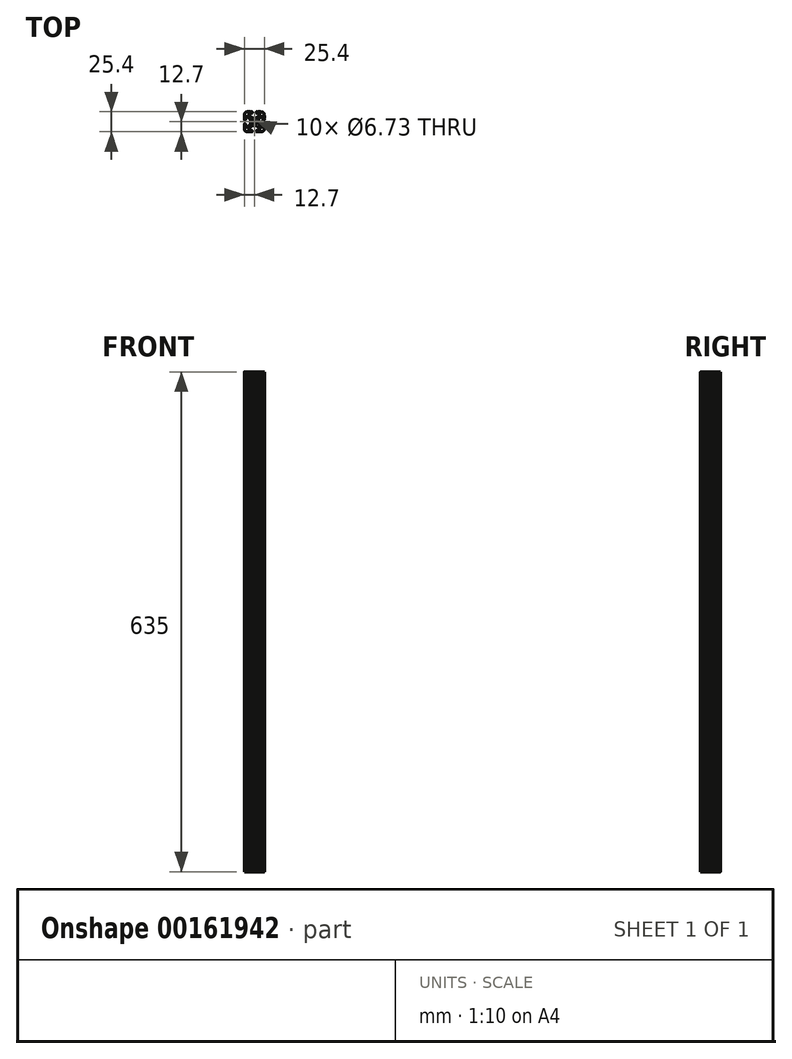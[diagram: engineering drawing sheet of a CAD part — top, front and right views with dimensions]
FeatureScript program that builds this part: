
annotation { "Feature Type Name" : "Feature", "Feature Type Description" : "" }
export const myFeature = defineFeature(function(context is Context, id is Id, definition is map)
    precondition{}
    {
        {
            var Q0;
            Q0=qCreatedBy(makeId("Top.planeOp"),FACE);
            var sketch = newSketch(context, id + "F0", { "sketchPlane" : qUnion([Q0])});
            skCircle(sketch, "E0", {"center": v(-12.7, 12.7) * mm, "radius": 3.36 * mm});
            skLineSegment(sketch, "E1.bottom", {"start": v(-11.24, 17.64) * mm, "end": v(-14.16, 17.64) * mm});
            skLineSegment(sketch, "E1.top", {"start": v(-11.24, 7.76) * mm, "end": v(-14.16, 7.76) * mm});
            skLineSegment(sketch, "E1.left", {"start": v(-7.76, 14.16) * mm, "end": v(-7.76, 11.24) * mm});
            skLineSegment(sketch, "E1.right", {"start": v(-17.64, 14.16) * mm, "end": v(-17.64, 11.24) * mm});
            skPoint(sketch, "E2.visualSharp", {"position": v(-25.4, 25.4) * mm});
            skPoint(sketch, "E3.visualSharp", {"position": v(0, 25.4) * mm});
            skPoint(sketch, "E4.visualSharp", {"position": v(0, 0) * mm});
            skPoint(sketch, "E5.visualSharp", {"position": v(-25.4, 0) * mm});
            skLineSegment(sketch, "E6.0", {"start": v(-18.7, 20.6) * mm, "end": v(-16.85, 18.76) * mm});
            skLineSegment(sketch, "E7.0", {"start": v(-20.6, 18.7) * mm, "end": v(-18.76, 16.85) * mm});
            skPoint(sketch, "E8.orphan", {"position": v(-23.85, 1.55) * mm});
            skPoint(sketch, "E9.orphan", {"position": v(-23.85, 23.85) * mm});
            skPoint(sketch, "E10.orphan", {"position": v(-1.55, 23.85) * mm});
            skPoint(sketch, "E11.orphan", {"position": v(-1.55, 1.55) * mm});
            skLineSegment(sketch, "E12", {"start": v(-8.55, 6.64) * mm, "end": v(-6.7, 4.8) * mm});
            skLineSegment(sketch, "E13.0", {"start": v(-18.7, 4.8) * mm, "end": v(-16.85, 6.64) * mm});
            skLineSegment(sketch, "E14.0", {"start": v(-20.6, 6.7) * mm, "end": v(-18.76, 8.55) * mm});
            skLineSegment(sketch, "E15.0", {"start": v(-8.55, 18.76) * mm, "end": v(-6.7, 20.6) * mm});
            skPoint(sketch, "E16.visualSharp", {"position": v(-23.85, 21.95) * mm});
            skArc(sketch, "E16.filletArc", {"start": v(-20.6, 18.7) * mm, "mid": v(-22.68, 19.1) * mm, "end": v(-23.85, 17.35) * mm});
            skPoint(sketch, "E17.visualSharp", {"position": v(-21.95, 23.85) * mm});
            skArc(sketch, "E17.filletArc", {"start": v(-17.35, 23.85) * mm, "mid": v(-19.1, 22.68) * mm, "end": v(-18.7, 20.6) * mm});
            skPoint(sketch, "E18.visualSharp", {"position": v(-5.34, 23.85) * mm});
            skLineSegment(sketch, "E19", {"start": v(-17.35, 23.85) * mm, "end": v(-15.58, 23.85) * mm});
            skLineSegment(sketch, "E20", {"start": v(-23.85, 17.35) * mm, "end": v(-23.85, 15.62) * mm});
            skLineSegment(sketch, "E21", {"start": v(-8.05, 1.55) * mm, "end": v(-9.78, 1.55) * mm});
            skArc(sketch, "E22.filletArc", {"start": v(-6.7, 20.6) * mm, "mid": v(-6.3, 22.68) * mm, "end": v(-8.05, 23.85) * mm});
            skPoint(sketch, "E23.visualSharp", {"position": v(-1.55, 3.45) * mm});
            skPoint(sketch, "E24.visualSharp", {"position": v(-3.45, 1.55) * mm});
            skArc(sketch, "E24.filletArc", {"start": v(-8.05, 1.55) * mm, "mid": v(-6.3, 2.73) * mm, "end": v(-6.7, 4.8) * mm});
            skArc(sketch, "E25.filletArc", {"start": v(-18.7, 4.8) * mm, "mid": v(-19.1, 2.73) * mm, "end": v(-17.35, 1.55) * mm});
            skArc(sketch, "E26.filletArc", {"start": v(-23.85, 8.05) * mm, "mid": v(-22.68, 6.3) * mm, "end": v(-20.6, 6.7) * mm});
            skLineSegment(sketch, "E27.bottom", {"start": v(-4.9, 0) * mm, "end": v(-8.05, 0) * mm});
            skLineSegment(sketch, "E27.top", {"start": v(-4.92, 25.4) * mm, "end": v(-8.05, 25.4) * mm});
            skLineSegment(sketch, "E27.left", {"start": v(0, 4.9) * mm, "end": v(0, 8.05) * mm});
            skLineSegment(sketch, "E27.right", {"start": v(-25.4, 4.9) * mm, "end": v(-25.4, 8.05) * mm});
            skArc(sketch, "E28.filletArc", {"start": v(-25.4, 3.81) * mm, "mid": v(-24.28, 1.12) * mm, "end": v(-21.59, 0) * mm});
            skArc(sketch, "E29.filletArc", {"start": v(-3.81, 0) * mm, "mid": v(-1.12, 1.12) * mm, "end": v(0, 3.8) * mm});
            skArc(sketch, "E30.filletArc", {"start": v(0, 21.59) * mm, "mid": v(-1.12, 24.28) * mm, "end": v(-3.8, 25.4) * mm});
            skArc(sketch, "E31.filletArc", {"start": v(-21.59, 25.4) * mm, "mid": v(-24.28, 24.28) * mm, "end": v(-25.4, 21.59) * mm});
            skPoint(sketch, "E32.newPointA", {"position": v(-17.64, 7.76) * mm});
            skArc(sketch, "E32.filletArc", {"start": v(-14.16, 7.76) * mm, "mid": v(-15.62, 7.47) * mm, "end": v(-16.85, 6.64) * mm});
            skPoint(sketch, "E33.newPointA", {"position": v(-7.76, 7.76) * mm});
            skArc(sketch, "E33.filletArc", {"start": v(-8.55, 6.64) * mm, "mid": v(-9.78, 7.47) * mm, "end": v(-11.24, 7.76) * mm});
            skArc(sketch, "E34.filletArc", {"start": v(-7.76, 11.24) * mm, "mid": v(-7.47, 9.78) * mm, "end": v(-6.64, 8.55) * mm});
            skArc(sketch, "E35.filletArc", {"start": v(-6.64, 16.85) * mm, "mid": v(-7.47, 15.62) * mm, "end": v(-7.76, 14.16) * mm});
            skPoint(sketch, "E36.newPointB", {"position": v(-7.76, 17.64) * mm});
            skArc(sketch, "E36.filletArc", {"start": v(-11.24, 17.64) * mm, "mid": v(-9.78, 17.93) * mm, "end": v(-8.55, 18.76) * mm});
            skPoint(sketch, "E37.newPointB", {"position": v(-17.64, 17.64) * mm});
            skArc(sketch, "E37.filletArc", {"start": v(-16.85, 18.76) * mm, "mid": v(-15.62, 17.93) * mm, "end": v(-14.16, 17.64) * mm});
            skArc(sketch, "E38.filletArc", {"start": v(-17.64, 14.16) * mm, "mid": v(-17.93, 15.62) * mm, "end": v(-18.76, 16.85) * mm});
            skArc(sketch, "E39.filletArc", {"start": v(-18.76, 8.55) * mm, "mid": v(-17.93, 9.78) * mm, "end": v(-17.64, 11.24) * mm});
            skLineSegment(sketch, "E40", {"start": v(-6.64, 8.55) * mm, "end": v(-4.8, 6.7) * mm});
            skPoint(sketch, "E41.visualSharp", {"position": v(-1.55, 21.95) * mm});
            skArc(sketch, "E42.filletArc", {"start": v(-4.8, 6.7) * mm, "mid": v(-2.73, 6.3) * mm, "end": v(-1.55, 8.05) * mm});
            skLineSegment(sketch, "E43", {"start": v(-1.55, 8.05) * mm, "end": v(-1.55, 9.78) * mm});
            skLineSegment(sketch, "E44", {"start": v(-6.64, 16.85) * mm, "end": v(-4.8, 18.7) * mm});
            skArc(sketch, "E45.filletArc", {"start": v(-1.55, 17.35) * mm, "mid": v(-2.73, 19.1) * mm, "end": v(-4.8, 18.7) * mm});
            skArc(sketch, "E46", {"start": v(-23.85, 9.78) * mm, "mid": v(-24.63, 10.56) * mm, "end": v(-25.4, 9.78) * mm});
            skArc(sketch, "E47", {"start": v(-25.4, 15.62) * mm, "mid": v(-24.63, 14.86) * mm, "end": v(-23.85, 15.62) * mm});
            skArc(sketch, "E48", {"start": v(-15.62, 23.85) * mm, "mid": v(-14.83, 24.63) * mm, "end": v(-15.62, 25.4) * mm});
            skArc(sketch, "E49", {"start": v(-9.78, 25.4) * mm, "mid": v(-10.6, 24.63) * mm, "end": v(-9.78, 23.85) * mm});
            skArc(sketch, "E50", {"start": v(-1.55, 15.62) * mm, "mid": v(-0.77, 14.88) * mm, "end": v(0, 15.62) * mm});
            skArc(sketch, "E51", {"start": v(0, 9.78) * mm, "mid": v(-0.77, 10.5) * mm, "end": v(-1.55, 9.78) * mm});
            skArc(sketch, "E52", {"start": v(-9.78, 1.55) * mm, "mid": v(-10.4, 0.77) * mm, "end": v(-9.78, 0) * mm});
            skArc(sketch, "E53", {"start": v(-15.62, 0) * mm, "mid": v(-14.85, 0.77) * mm, "end": v(-15.62, 1.55) * mm});
            skLineSegment(sketch, "E54.trimOffspring", {"start": v(-15.62, 1.55) * mm, "end": v(-17.35, 1.55) * mm});
            skLineSegment(sketch, "E55.trimOffspring", {"start": v(-16.7, 0) * mm, "end": v(-20.5, 0) * mm});
            skLineSegment(sketch, "E56.trimOffspring", {"start": v(-1.55, 15.62) * mm, "end": v(-1.55, 17.35) * mm});
            skLineSegment(sketch, "E57.trimOffspring", {"start": v(0, 15.62) * mm, "end": v(0, 16.26) * mm});
            skLineSegment(sketch, "E58.trimOffspring", {"start": v(-23.85, 9.78) * mm, "end": v(-23.85, 8.05) * mm});
            skLineSegment(sketch, "E59.trimOffspring", {"start": v(-25.4, 15.62) * mm, "end": v(-25.4, 16.26) * mm});
            skLineSegment(sketch, "E60.trimOffspring", {"start": v(-9.86, 23.85) * mm, "end": v(-8.05, 23.85) * mm});
            skLineSegment(sketch, "E61.trimOffspring", {"start": v(-15.58, 25.4) * mm, "end": v(-16.25, 25.4) * mm});
            skPoint(sketch, "E62.start.orphan", {"position": v(-15.62, 17.93) * mm});
            skPoint(sketch, "E63.start.orphan", {"position": v(-9.78, 17.93) * mm});
            skPoint(sketch, "E64.start.orphan", {"position": v(-7.47, 15.62) * mm});
            skPoint(sketch, "E65.start.orphan", {"position": v(-7.47, 9.78) * mm});
            skPoint(sketch, "E66.start.orphan", {"position": v(-17.93, 15.62) * mm});
            skPoint(sketch, "E67.start.orphan", {"position": v(-17.93, 9.78) * mm});
            skPoint(sketch, "E68.start.orphan", {"position": v(-9.78, 7.47) * mm});
            skPoint(sketch, "E69.start.orphan", {"position": v(-15.62, 7.47) * mm});
            skPoint(sketch, "E70.endSnap0", {"position": v(0, 18.6) * mm});
            skPoint(sketch, "E71.startSnap0", {"position": v(-1.55, 8.92) * mm});
            skArc(sketch, "E72", {"start": v(-4.92, 25.4) * mm, "mid": v(-4.37, 24.9) * mm, "end": v(-3.81, 25.4) * mm});
            skArc(sketch, "E73", {"start": v(-9.14, 25.4) * mm, "mid": v(-8.6, 24.86) * mm, "end": v(-8.05, 25.4) * mm});
            skArc(sketch, "E74", {"start": v(-17.35, 25.4) * mm, "mid": v(-16.8, 24.86) * mm, "end": v(-16.25, 25.4) * mm});
            skArc(sketch, "E75", {"start": v(-21.59, 25.4) * mm, "mid": v(-21.04, 24.85) * mm, "end": v(-20.49, 25.4) * mm});
            skLineSegment(sketch, "E76", {"start": v(-25.4, 21.59) * mm, "end": v(-25.4, 20.5) * mm});
            skArc(sketch, "E77", {"start": v(-25.4, 16.26) * mm, "mid": v(-24.84, 16.8) * mm, "end": v(-25.4, 17.35) * mm});
            skArc(sketch, "E78", {"start": v(-25.4, 8.05) * mm, "mid": v(-24.9, 8.6) * mm, "end": v(-25.4, 9.15) * mm});
            skArc(sketch, "E79", {"start": v(-25.4, 3.81) * mm, "mid": v(-24.85, 4.36) * mm, "end": v(-25.4, 4.9) * mm});
            skArc(sketch, "E80", {"start": v(-20.5, 0) * mm, "mid": v(-21.04, 0.55) * mm, "end": v(-21.59, 0) * mm});
            skArc(sketch, "E81", {"start": v(-15.62, 0) * mm, "mid": v(-16.16, 0.54) * mm, "end": v(-16.7, 0) * mm});
            skArc(sketch, "E82", {"start": v(-8.05, 0) * mm, "mid": v(-8.6, 0.55) * mm, "end": v(-9.15, 0) * mm});
            skArc(sketch, "E83", {"start": v(-3.81, 0) * mm, "mid": v(-4.35, 0.54) * mm, "end": v(-4.9, 0) * mm});
            skLineSegment(sketch, "E84.trimOffspring", {"start": v(-17.35, 25.4) * mm, "end": v(-20.49, 25.4) * mm});
            skLineSegment(sketch, "E85.trimOffspring", {"start": v(-25.4, 17.35) * mm, "end": v(-25.4, 21.59) * mm});
            skLineSegment(sketch, "E86.trimOffspring", {"start": v(-25.4, 9.15) * mm, "end": v(-25.4, 9.78) * mm});
            skLineSegment(sketch, "E87.trimOffspring", {"start": v(-9.15, 0) * mm, "end": v(-9.78, 0) * mm});
            skArc(sketch, "E88", {"start": v(0, 4.9) * mm, "mid": v(-0.54, 4.36) * mm, "end": v(0, 3.8) * mm});
            skArc(sketch, "E89", {"start": v(0, 9.15) * mm, "mid": v(-0.54, 8.6) * mm, "end": v(0, 8.05) * mm});
            skLineSegment(sketch, "E90.trimOffspring", {"start": v(0, 9.15) * mm, "end": v(0, 9.78) * mm});
            skArc(sketch, "E91", {"start": v(0, 21.59) * mm, "mid": v(-0.55, 21.04) * mm, "end": v(0, 20.5) * mm});
            skArc(sketch, "E92", {"start": v(0, 17.35) * mm, "mid": v(-0.55, 16.8) * mm, "end": v(0, 16.26) * mm});
            skLineSegment(sketch, "E93.trimOffspring", {"start": v(0, 17.35) * mm, "end": v(0, 20.5) * mm});
            skLineSegment(sketch, "E94.trimOffspring", {"start": v(-9.14, 25.4) * mm, "end": v(-9.86, 25.4) * mm});
            skSolve(sketch);
        }
        {
            var Q0;
            Q0=qSketchRegion(id+"F0",true);
            extrude(context, id + "F1", {"entities" : qUnion([Q0]), "depth" : 635 * mm});
        }
    });
